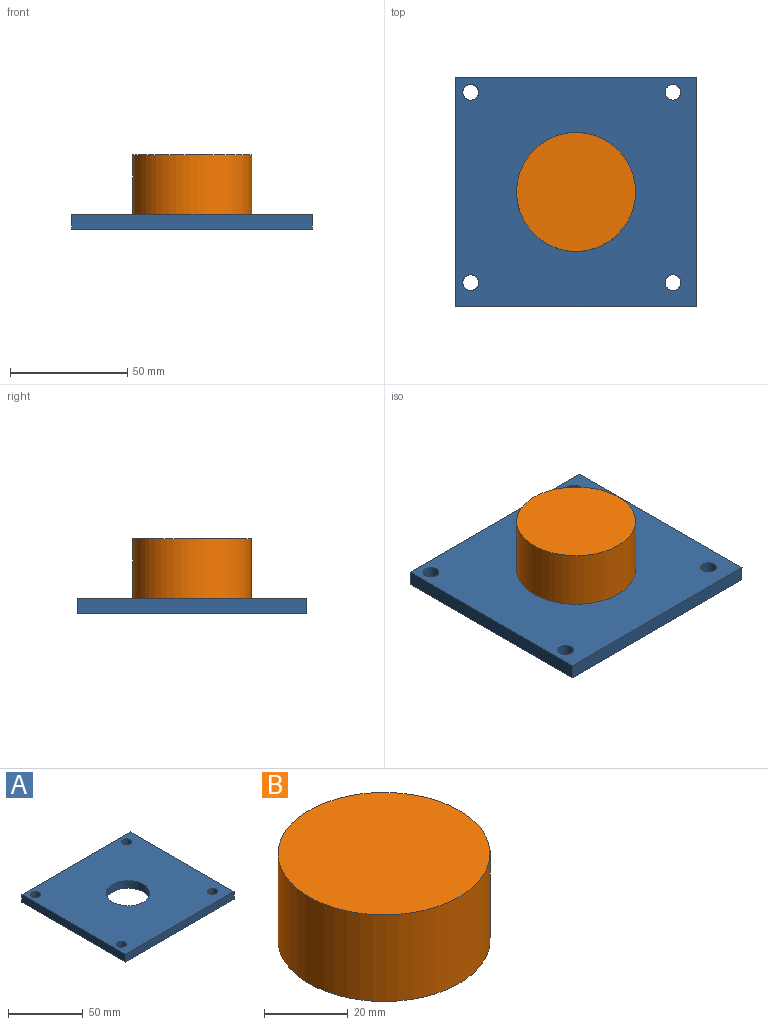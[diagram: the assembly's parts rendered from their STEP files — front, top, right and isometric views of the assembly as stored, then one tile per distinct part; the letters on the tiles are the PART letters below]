
ASSEMBLY  parts=2 mates=1
PART A: 11 faces, bbox 102.6x97.8x6.4 mm
  f0: plane 102.63x6.35mm, normal (0,-1,0), area 651.7mm2, adj f1,f3,f4,f5
  f1: plane 97.83x6.35mm, normal (1,0,0), area 621.2mm2, adj f0,f2,f4,f5
  f2: plane 102.63x6.35mm, normal (0,1,0), area 651.7mm2, adj f1,f3,f4,f5
  f3: plane 97.83x6.35mm, normal (-1,0,0), area 621.2mm2, adj f0,f2,f4,f5
  f4: plane 102.63x97.83mm, normal (0,0,1), area 9232.4mm2, adj f0,f1,f2,f3,f6,f7,f8,f9
  f5: plane 102.63x97.83mm, normal (0,0,-1), area 9232.4mm2, adj f0,f1,f2,f3,f6,f7,f8,f9
  f6: cylinder r=3.38mm len=6.76mm, axis (0,0,-1), area 134.8mm2, adj f4,f5
  f7: cylinder r=3.38mm len=6.76mm, axis (0,0,-1), area 134.8mm2, adj f4,f5
  f8: cylinder r=3.38mm len=6.76mm, axis (0,0,-1), area 134.8mm2, adj f4,f5
  f9: cylinder r=3.38mm len=6.76mm, axis (0,0,-1), area 134.8mm2, adj f4,f5
  f10: cylinder r=14.54mm len=29.08mm, axis (0,0,1), area 580.1mm2, adj f4,f5
PART B: 3 faces, bbox 50.8x50.8x25.4 mm
  f0: cylinder r=25.4mm len=50.8mm, axis (0,0,-1), area 4053.7mm2, adj f1,f2
  f1: plane 50.8x50.8mm, normal (0,0,1), area 2026.8mm2, adj f0
  f2: plane 50.8x50.8mm, normal (0,0,-1), area 2026.8mm2, adj f0
PLACE A rot(axis=(0.72,-0.22,-0.65),0deg) t=(-74.65,-33.07,-11.18)mm
PLACE B rot(axis=(0.72,-0.22,-0.65),0deg) t=(-74.63,-33.1,-4.83)mm
MATE fastened A.f4 <-> B.f0  axis (0,0,1) through (-74.63,-33.1,-4.83)mm
